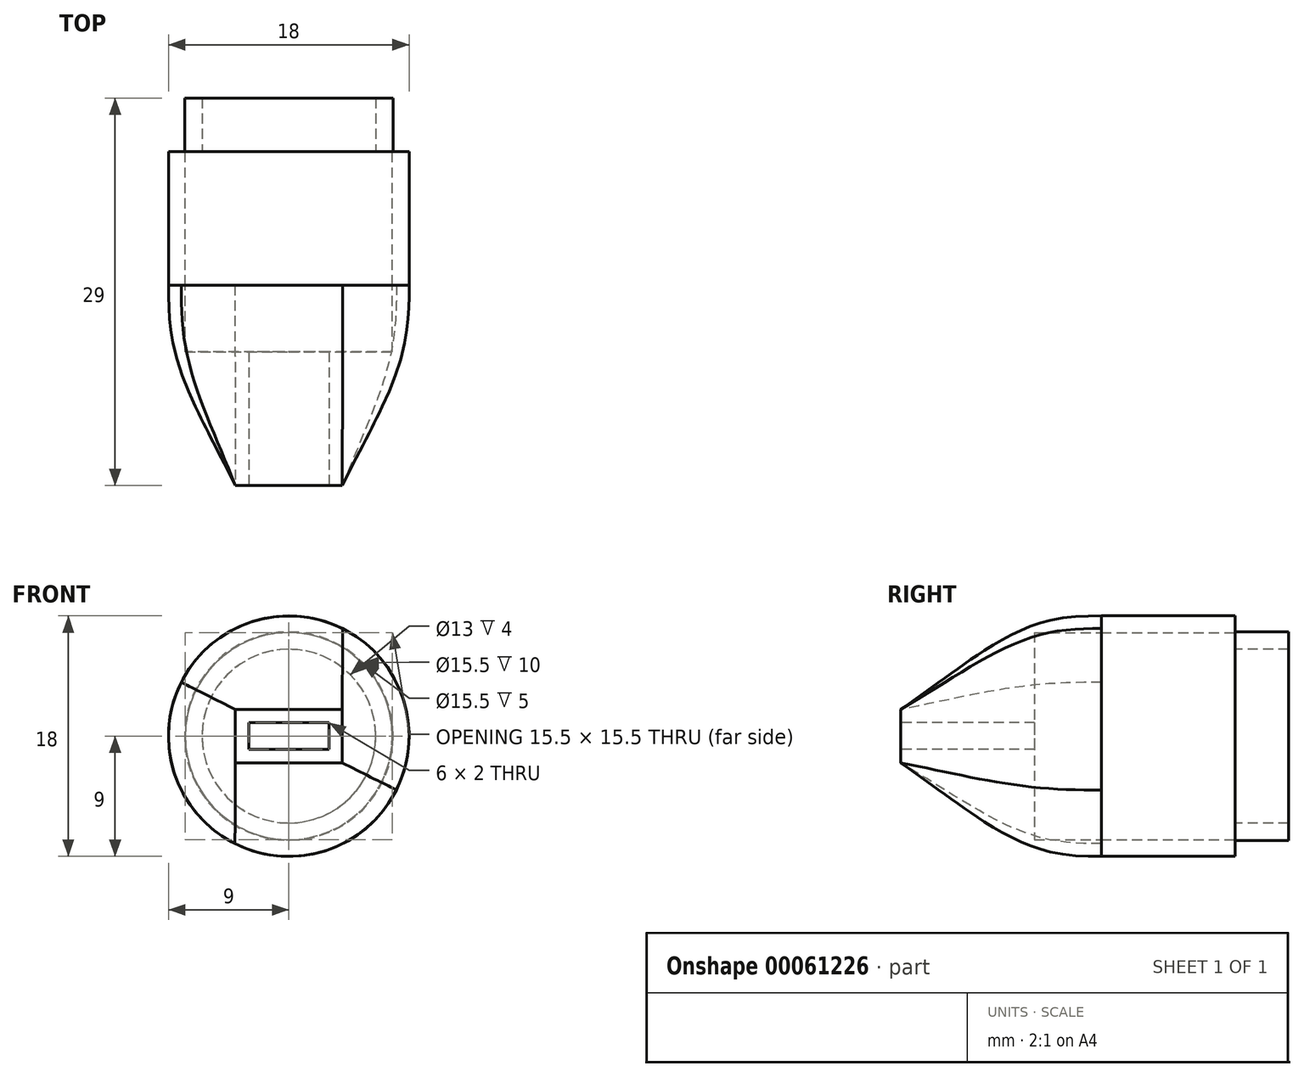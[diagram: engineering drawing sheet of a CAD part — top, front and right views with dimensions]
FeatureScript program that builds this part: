
annotation { "Feature Type Name" : "Feature", "Feature Type Description" : "" }
export const myFeature = defineFeature(function(context is Context, id is Id, definition is map)
    precondition{}
    {
        {
            var Q0;
            Q0=qCreatedBy(makeId("Front.planeOp"),FACE);
            var sketch = newSketch(context, id + "F0", { "sketchPlane" : qUnion([Q0])});
            skCircle(sketch, "E0", {"center": v(0, 0) * mm, "radius": 7.8 * mm});
            skSolve(sketch);
        }
        {
            var Q0;
            Q0 = qSketchRegion(id + "F0", true);
            extrude(context, id + "F1", {"entities" : qUnion([Q0]), "depth" : 4 * mm});
        }
        {
            var Q0;
            Q0=makeQuery(id+"F1.opExtrude","CAP_FACE",FACE,{"disambiguationData":[OSD([sQuery(id+"F0.wireOp",EDGE,"E0")])],"isStart":false});
            var sketch = newSketch(context, id + "F2", { "sketchPlane" : qUnion([Q0])});
            skCircle(sketch, "E1", {"center": v(0, 0) * mm, "radius": 6.5 * mm});
            skSolve(sketch);
        }
        {
            var Q0;
            Q0 = qSketchRegion(id + "F2", true);
            extrude(context, id + "F3", {"entities" : qUnion([Q0]), "operationType" : NewBodyOperationType.REMOVE, "endBound" : BoundingType.THROUGH_ALL, "oppositeDirection" : true, "depth" : 25 * mm});
        }
        {
            var Q0;
            Q0=makeQuery(id+"F1.opExtrude","CAP_FACE",FACE,{"disambiguationData":[OSD([sQuery(id+"F0.wireOp",EDGE,"E0")])],"isStart":false});
            var sketch = newSketch(context, id + "F4", { "sketchPlane" : qUnion([Q0])});
            skCircle(sketch, "E2", {"center": v(0, 0) * mm, "radius": 9 * mm});
            skSolve(sketch);
        }
        {
            var Q0;
            Q0 = qSketchRegion(id + "F4", true);
            extrude(context, id + "F5", {"entities" : qUnion([Q0]), "operationType" : NewBodyOperationType.ADD, "depth" : 10 * mm});
        }
        {
            var Q0;
            Q0=makeQuery(id+"F5.opExtrude","CAP_FACE",FACE,{"disambiguationData":[OSD([sQuery(id+"F4.wireOp",EDGE,"E2")])],"isStart":false});
            cPlane(context, id + "F6", {"entities" : qUnion([Q0]), "cplaneType" : CPlaneType.OFFSET, "offset" : 15 * mm, "width" : 150 * mm, "height" : 150 * mm});
        }
        {
            var Q0;
            Q0=qCreatedBy(id+"F6.planeOp",FACE);
            var sketch = newSketch(context, id + "F7", { "sketchPlane" : qUnion([Q0])});
            skLineSegment(sketch, "E3.rect.bottom", {"start": v(4, -2) * mm, "end": v(-4, -2) * mm});
            skLineSegment(sketch, "E3.rect.top", {"start": v(4, 2) * mm, "end": v(-4, 2) * mm});
            skLineSegment(sketch, "E3.rect.left", {"start": v(4, -2) * mm, "end": v(4, 2) * mm});
            skLineSegment(sketch, "E3.rect.right", {"start": v(-4, -2) * mm, "end": v(-4, 2) * mm});
            skPoint(sketch, "E3.rect.middle", {"position": v(0, 0) * mm});
            skSolve(sketch);
        }
        {
            var Q0;
            Q0=makeQuery(id+"F5.opExtrude","CAP_FACE",FACE,{"disambiguationData":[OSD([sQuery(id+"F4.wireOp",EDGE,"E2")])],"isStart":false});
            var Q1;
            Q1=makeQuery(id+"F7.imprint","IMPRINT",FACE,{"disambiguationData":[TD([[makeQuery(id+"F7.imprint","IMPRINT",EDGE,{"derivedFrom":sQuery(id+"F7.wireOp",EDGE,"E3.rect.bottom")}),-1.0]])]});
            loft(context, id + "F8", {"startCondition" : LoftEndDerivativeType.MATCH_CURVATURE, "startMagnitude" : 1, "sheetProfilesArray" : [{ "sheetProfileEntities" : qUnion([Q0]) }, { "sheetProfileEntities" : qUnion([Q1]) }]});
        }
        {
            var Q0;
            Q0=makeQuery(id+"F8.opLoft","CAP_FACE",FACE,{"disambiguationData":[OSD([makeQuery(id+"F7.imprint","IMPRINT",FACE,{"disambiguationData":[TD([[makeQuery(id+"F7.imprint","IMPRINT",EDGE,{"derivedFrom":sQuery(id+"F7.wireOp",EDGE,"E3.rect.bottom")}),-1.0]])]})])],"isStart":true});
            var sketch = newSketch(context, id + "F9", { "sketchPlane" : qUnion([Q0])});
            skLineSegment(sketch, "E4.rect.bottom", {"start": v(3, 1) * mm, "end": v(-3, 1) * mm});
            skLineSegment(sketch, "E4.rect.top", {"start": v(3, -1) * mm, "end": v(-3, -1) * mm});
            skLineSegment(sketch, "E4.rect.left", {"start": v(3, 1) * mm, "end": v(3, -1) * mm});
            skLineSegment(sketch, "E4.rect.right", {"start": v(-3, 1) * mm, "end": v(-3, -1) * mm});
            skPoint(sketch, "E4.rect.middle", {"position": v(0, 0) * mm});
            skSolve(sketch);
        }
        {
            var Q0;
            Q0 = qSketchRegion(id + "F9", true);
            extrude(context, id + "F10", {"entities" : qUnion([Q0]), "operationType" : NewBodyOperationType.REMOVE, "endBound" : BoundingType.THROUGH_ALL, "oppositeDirection" : true, "depth" : 25 * mm});
        }
        {
            var Q0;
            Q0=makeQuery(id+"F5.boolean.opBoolean","SPLIT",FACE,{"disambiguationData":[TD([makeQuery(id+"F3.boolean.opBoolean","COPY",FACE,{"derivedFrom":makeQuery(id+"F3.opExtrude","SWEPT_FACE",FACE,{"disambiguationData":[OSD([sQuery(id+"F2.wireOp",EDGE,"E1")])]})})])],"derivedFrom":makeQuery(id+"F5.opExtrude","CAP_FACE",FACE,{"disambiguationData":[OSD([sQuery(id+"F4.wireOp",EDGE,"E2")])],"isStart":true})});
            var sketch = newSketch(context, id + "F11", { "sketchPlane" : qUnion([Q0])});
            skCircle(sketch, "E5", {"center": v(0, 0) * mm, "radius": 7.75 * mm});
            skSolve(sketch);
        }
        {
            var Q0;
            Q0 = qSketchRegion(id + "F11", true);
            extrude(context, id + "F12", {"entities" : qUnion([Q0]), "operationType" : NewBodyOperationType.REMOVE, "oppositeDirection" : true, "depth" : 15 * mm});
        }
    });
